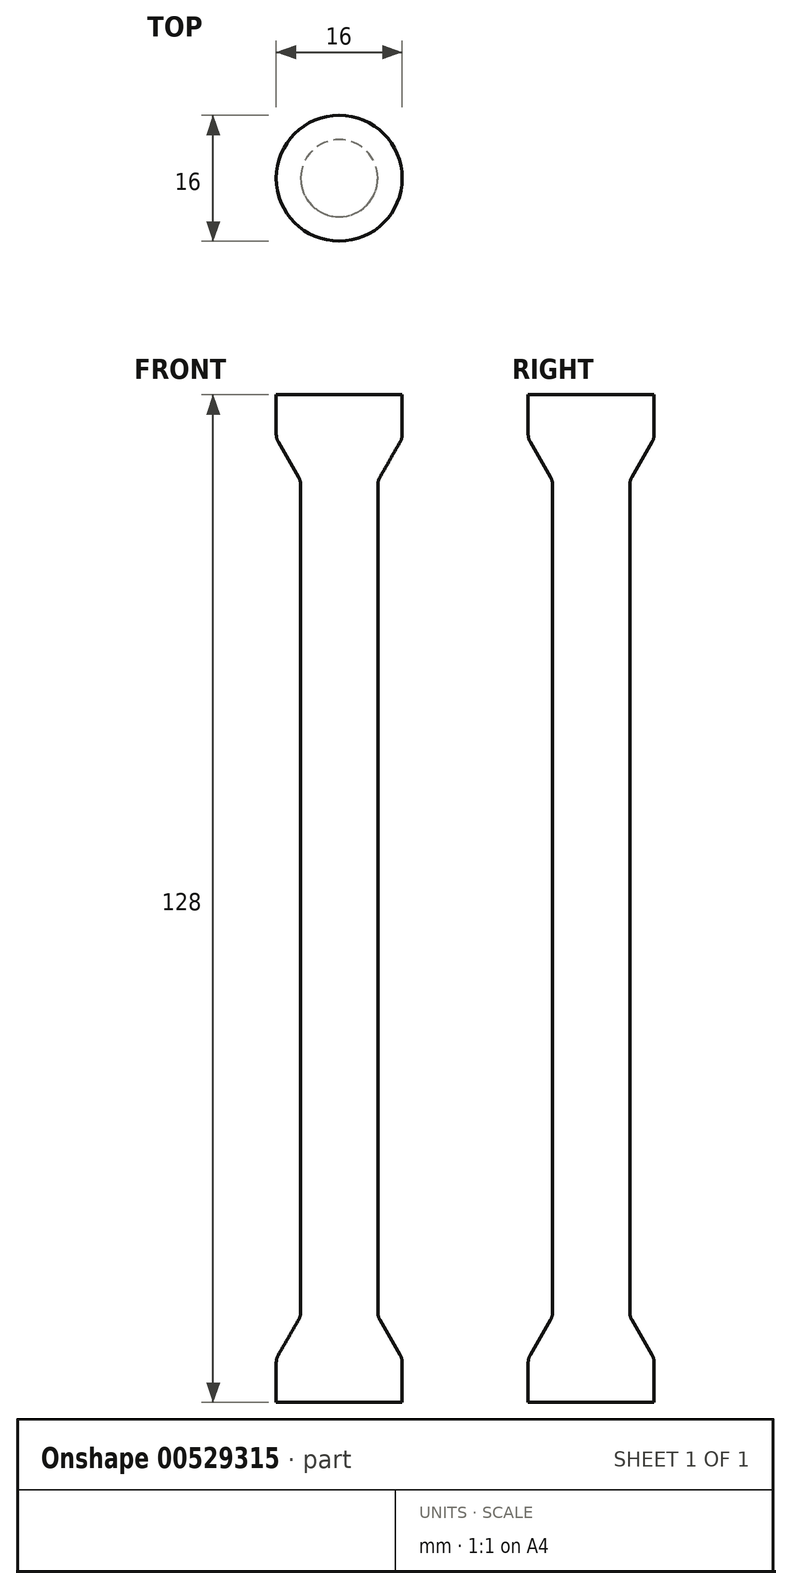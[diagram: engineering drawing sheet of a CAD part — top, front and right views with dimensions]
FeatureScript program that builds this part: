
annotation { "Feature Type Name" : "Feature", "Feature Type Description" : "" }
export const myFeature = defineFeature(function(context is Context, id is Id, definition is map)
    precondition{}
    {
        {
            var Q0;
            Q0=qCreatedBy(makeId("Front.planeOp"),FACE);
            var sketch = newSketch(context, id + "F0", { "sketchPlane" : qUnion([Q0])});
            skLineSegment(sketch, "E0.bottom", {"start": v(0, 0) * mm, "end": v(4.9, 0) * mm});
            skLineSegment(sketch, "E0.top", {"start": v(0, 60) * mm, "end": v(4.9, 60) * mm});
            skLineSegment(sketch, "E0.left", {"start": v(0, 0) * mm, "end": v(0, 60) * mm});
            skLineSegment(sketch, "E0.right", {"start": v(4.9, 0) * mm, "end": v(4.9, 60) * mm});
            skLineSegment(sketch, "E1.bottom", {"start": v(0, 60) * mm, "end": v(8, 60) * mm});
            skLineSegment(sketch, "E1.top", {"start": v(0, 64) * mm, "end": v(8, 64) * mm});
            skLineSegment(sketch, "E1.left", {"start": v(0, 60) * mm, "end": v(0, 64) * mm});
            skLineSegment(sketch, "E1.right", {"start": v(8, 60) * mm, "end": v(8, 64) * mm});
            skLineSegment(sketch, "E2.MirrorCS", {"start": v(8, -60) * mm, "end": v(8, -64) * mm});
            skLineSegment(sketch, "E3.MirrorCS", {"start": v(0, -60) * mm, "end": v(0, -64) * mm});
            skLineSegment(sketch, "E4.MirrorCS", {"start": v(0, -60) * mm, "end": v(4.9, -60) * mm});
            skLineSegment(sketch, "E5.MirrorCS", {"start": v(0, -60) * mm, "end": v(8, -60) * mm});
            skLineSegment(sketch, "E6.MirrorCS", {"start": v(0, 0) * mm, "end": v(0, -60) * mm});
            skLineSegment(sketch, "E7.MirrorCS", {"start": v(0, -64) * mm, "end": v(8, -64) * mm});
            skLineSegment(sketch, "E8.MirrorCS", {"start": v(4.9, 0) * mm, "end": v(4.9, -60) * mm});
            skSolve(sketch);
        }
        {
            var Q0;
            Q0=makeQuery(id+"F0.imprint","IMPRINT",FACE,{"disambiguationData":[TD([[makeQuery(id+"F0.imprint","IMPRINT",EDGE,{"derivedFrom":sQuery(id+"F0.wireOp",EDGE,"E1.top")}),-1.0]])]});
            var Q1;
            {var subQ0=sQuery(id+"F0.wireOp",EDGE,"E0.left");Q1=makeQuery(id+"F0.imprint","IMPRINT",FACE,{"disambiguationData":[TD([[makeQuery(id+"F0.imprint","IMPRINT",EDGE,{"derivedFrom":subQ0}),-1.0]])]});}
            var Q2;
            Q2=makeQuery(id+"F0.imprint","IMPRINT",FACE,{"disambiguationData":[TD([[makeQuery(id+"F0.imprint","IMPRINT",EDGE,{"derivedFrom":sQuery(id+"F0.wireOp",EDGE,"E0.bottom")}),-1.0]])]});
            var Q3;
            {var subQ1=sQuery(id+"F0.wireOp",EDGE,"E2.MirrorCS");Q3=makeQuery(id+"F0.imprint","IMPRINT",FACE,{"disambiguationData":[TD([[makeQuery(id+"F0.imprint","IMPRINT",EDGE,{"derivedFrom":subQ1}),-1.0]])]});}
            var Q4;
            Q4=sQuery(id+"F0.wireOp",EDGE,"E6.MirrorCS");
            revolve(context, id + "F1", {"entities" : qUnion([Q0, Q1, Q2, Q3]), "axis" : qUnion([Q4]), "revolveType" : RevolveType.FULL});
        }
        {
            var Q0;
            Q0=makeQuery(id+"F1.opRevolve","SWEPT_EDGE",EDGE,{"disambiguationData":[OSD([sQuery(id+"F0.wireOp",EDGE,"E0.right"),sQuery(id+"F0.wireOp",EDGE,"E1.bottom")])]});
            chamfer(context, id + "F2", {"entities" : qUnion([Q0]), "chamferType" : ChamferType.OFFSET_ANGLE, "width" : 4 * mm, "oppositeDirection" : false, "angle" : 60 * degree, "tangentPropagation" : true});
        }
        {
            var Q0;
            Q0=makeQuery(id+"F1.opRevolve","SWEPT_EDGE",EDGE,{"disambiguationData":[OSD([sQuery(id+"F0.wireOp",EDGE,"E5.MirrorCS"),sQuery(id+"F0.wireOp",EDGE,"E8.MirrorCS")])]});
            chamfer(context, id + "F3", {"entities" : qUnion([Q0]), "chamferType" : ChamferType.OFFSET_ANGLE, "width" : 4 * mm, "oppositeDirection" : true, "angle" : 60 * degree, "tangentPropagation" : true});
        }
        {
            var Q0;
            Q0=makeQuery(id+"F2.opChamfer","BLEND_EDGE",EDGE,{"blendedFrom":[makeQuery(id+"F1.opRevolve","SWEPT_EDGE",EDGE,{"disambiguationData":[OSD([sQuery(id+"F0.wireOp",EDGE,"E0.right"),sQuery(id+"F0.wireOp",EDGE,"E1.bottom")])]}),makeQuery(id+"F1.opRevolve","SWEPT_FACE",FACE,{"disambiguationData":[OSD([sQuery(id+"F0.wireOp",EDGE,"E1.right")])]})],"blendedInto":[makeQuery(id+"F1.opRevolve","SWEPT_FACE",FACE,{"disambiguationData":[OSD([sQuery(id+"F0.wireOp",EDGE,"E1.right")])]})]});
            var Q1;
            Q1=makeQuery(id+"F3.opChamfer","BLEND_EDGE",EDGE,{"blendedFrom":[makeQuery(id+"F1.opRevolve","SWEPT_EDGE",EDGE,{"disambiguationData":[OSD([sQuery(id+"F0.wireOp",EDGE,"E5.MirrorCS"),sQuery(id+"F0.wireOp",EDGE,"E8.MirrorCS")])]}),makeQuery(id+"F1.opRevolve","SWEPT_FACE",FACE,{"disambiguationData":[OSD([sQuery(id+"F0.wireOp",EDGE,"E2.MirrorCS")])]})],"blendedInto":[makeQuery(id+"F1.opRevolve","SWEPT_FACE",FACE,{"disambiguationData":[OSD([sQuery(id+"F0.wireOp",EDGE,"E2.MirrorCS")])]})]});
            var Q2;
            {var subQ0=sQuery(id+"F0.wireOp",EDGE,"E0.right");Q2=makeQuery(id+"F2.opChamfer","BLEND_EDGE",EDGE,{"blendedFrom":[makeQuery(id+"F1.opRevolve","SWEPT_EDGE",EDGE,{"disambiguationData":[OSD([subQ0,sQuery(id+"F0.wireOp",EDGE,"E1.bottom")])]}),makeQuery(id+"F1.opRevolve","SWEPT_FACE",FACE,{"disambiguationData":[OSD([subQ0,sQuery(id+"F0.wireOp",EDGE,"E8.MirrorCS")])]})],"blendedInto":[makeQuery(id+"F1.opRevolve","SWEPT_FACE",FACE,{"disambiguationData":[OSD([subQ0,sQuery(id+"F0.wireOp",EDGE,"E8.MirrorCS")])]})]});}
            var Q3;
            {var subQ0=sQuery(id+"F0.wireOp",EDGE,"E8.MirrorCS");Q3=makeQuery(id+"F3.opChamfer","BLEND_EDGE",EDGE,{"blendedFrom":[makeQuery(id+"F1.opRevolve","SWEPT_EDGE",EDGE,{"disambiguationData":[OSD([sQuery(id+"F0.wireOp",EDGE,"E5.MirrorCS"),subQ0])]}),makeQuery(id+"F1.opRevolve","SWEPT_FACE",FACE,{"disambiguationData":[OSD([sQuery(id+"F0.wireOp",EDGE,"E0.right"),subQ0])]})],"blendedInto":[makeQuery(id+"F1.opRevolve","SWEPT_FACE",FACE,{"disambiguationData":[OSD([sQuery(id+"F0.wireOp",EDGE,"E0.right"),subQ0])]})]});}
            fillet(context, id + "F4", {"entities" : qUnion([Q0, Q1, Q2, Q3]), "radius" : 2 * mm, "tangentPropagation" : true, "allowEdgeOverflow" : false});
        }
    });
